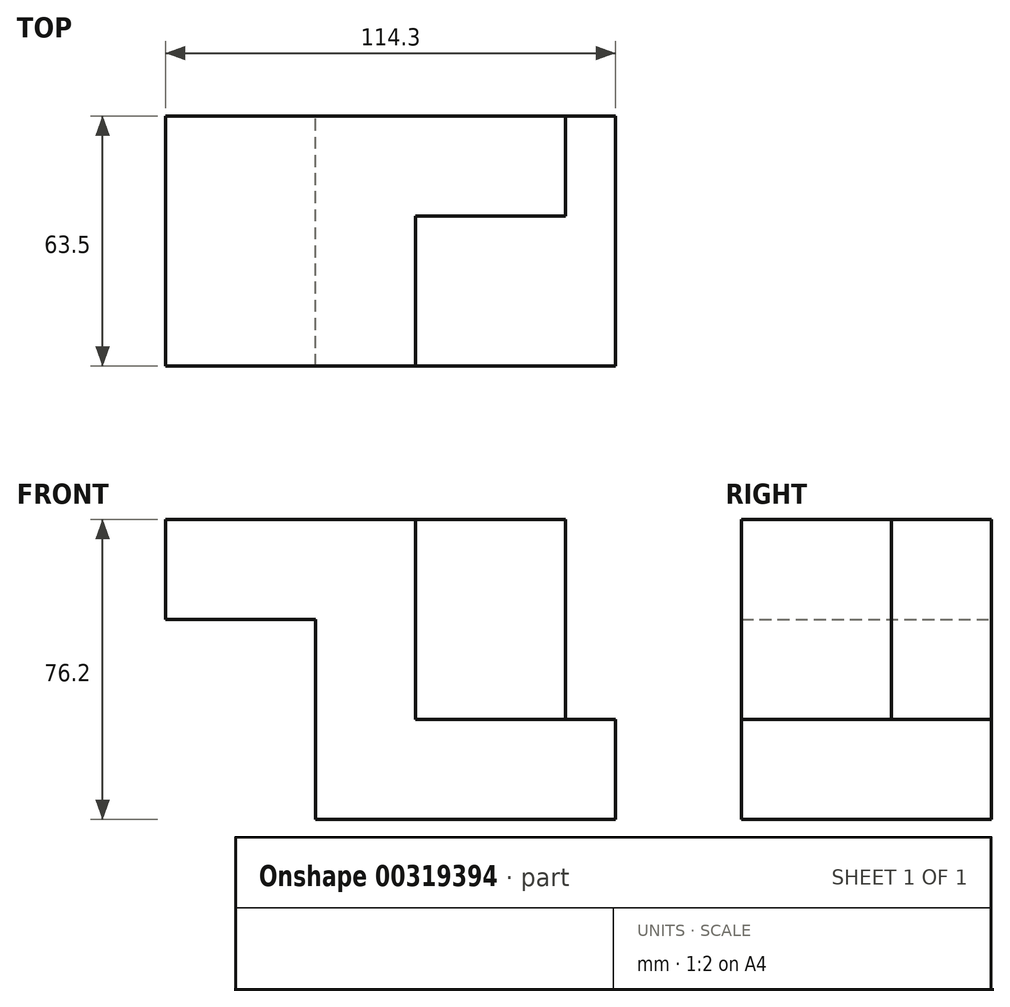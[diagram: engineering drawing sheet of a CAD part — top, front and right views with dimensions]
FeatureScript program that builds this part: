
annotation { "Feature Type Name" : "Feature", "Feature Type Description" : "" }
export const myFeature = defineFeature(function(context is Context, id is Id, definition is map)
    precondition{}
    {
        {
            var Q0;
            Q0=qCreatedBy(makeId("Front.planeOp"),FACE);
            var sketch = newSketch(context, id + "F0", { "sketchPlane" : qUnion([Q0])});
            skLineSegment(sketch, "E0", {"start": v(69.84, -22.45) * mm, "end": v(-6.36, -22.45) * mm});
            skLineSegment(sketch, "E1", {"start": v(-6.36, -22.45) * mm, "end": v(-6.36, 28.35) * mm});
            skLineSegment(sketch, "E2", {"start": v(-6.36, 28.35) * mm, "end": v(-44.46, 28.35) * mm});
            skLineSegment(sketch, "E3", {"start": v(-44.46, 28.35) * mm, "end": v(-44.46, 53.75) * mm});
            skLineSegment(sketch, "E4", {"start": v(-44.46, 53.75) * mm, "end": v(19.04, 53.75) * mm});
            skLineSegment(sketch, "E5", {"start": v(19.04, 53.75) * mm, "end": v(19.04, 2.95) * mm});
            skLineSegment(sketch, "E6", {"start": v(19.04, 2.95) * mm, "end": v(69.84, 2.95) * mm});
            skLineSegment(sketch, "E7", {"start": v(69.84, 2.95) * mm, "end": v(69.84, -22.45) * mm});
            skSolve(sketch);
        }
        {
            var Q0;
            Q0=makeQuery(id+"F0.imprint","IMPRINT",FACE,{"disambiguationData":[TD([[makeQuery(id+"F0.imprint","IMPRINT",EDGE,{"derivedFrom":sQuery(id+"F0.wireOp",EDGE,"E0")}),-1.0]])]});
            extrude(context, id + "F1", {"entities" : qUnion([Q0]), "depth" : 63.5 * mm});
        }
        {
            var Q0;
            Q0=makeQuery(id+"F1.opExtrude","SWEPT_FACE",FACE,{"disambiguationData":[OSD([sQuery(id+"F0.wireOp",EDGE,"E4")])]});
            var sketch = newSketch(context, id + "F2", { "sketchPlane" : qUnion([Q0])});
            skLineSegment(sketch, "E8.bottom", {"start": v(19.04, 0) * mm, "end": v(57.14, 0) * mm});
            skLineSegment(sketch, "E8.top", {"start": v(19.04, -25.4) * mm, "end": v(57.14, -25.4) * mm});
            skLineSegment(sketch, "E8.left", {"start": v(19.04, 0) * mm, "end": v(19.04, -25.4) * mm});
            skLineSegment(sketch, "E8.right", {"start": v(57.14, 0) * mm, "end": v(57.14, -25.4) * mm});
            skSolve(sketch);
        }
        {
            var Q0;
            Q0=makeQuery(id+"F2.imprint","IMPRINT",FACE,{"disambiguationData":[TD([[makeQuery(id+"F2.imprint","IMPRINT",EDGE,{"derivedFrom":sQuery(id+"F2.wireOp",EDGE,"E8.bottom")}),-1.0]])]});
            extrude(context, id + "F3", {"entities" : qUnion([Q0]), "operationType" : NewBodyOperationType.ADD, "oppositeDirection" : true, "depth" : 66.55 * mm});
        }
    });
